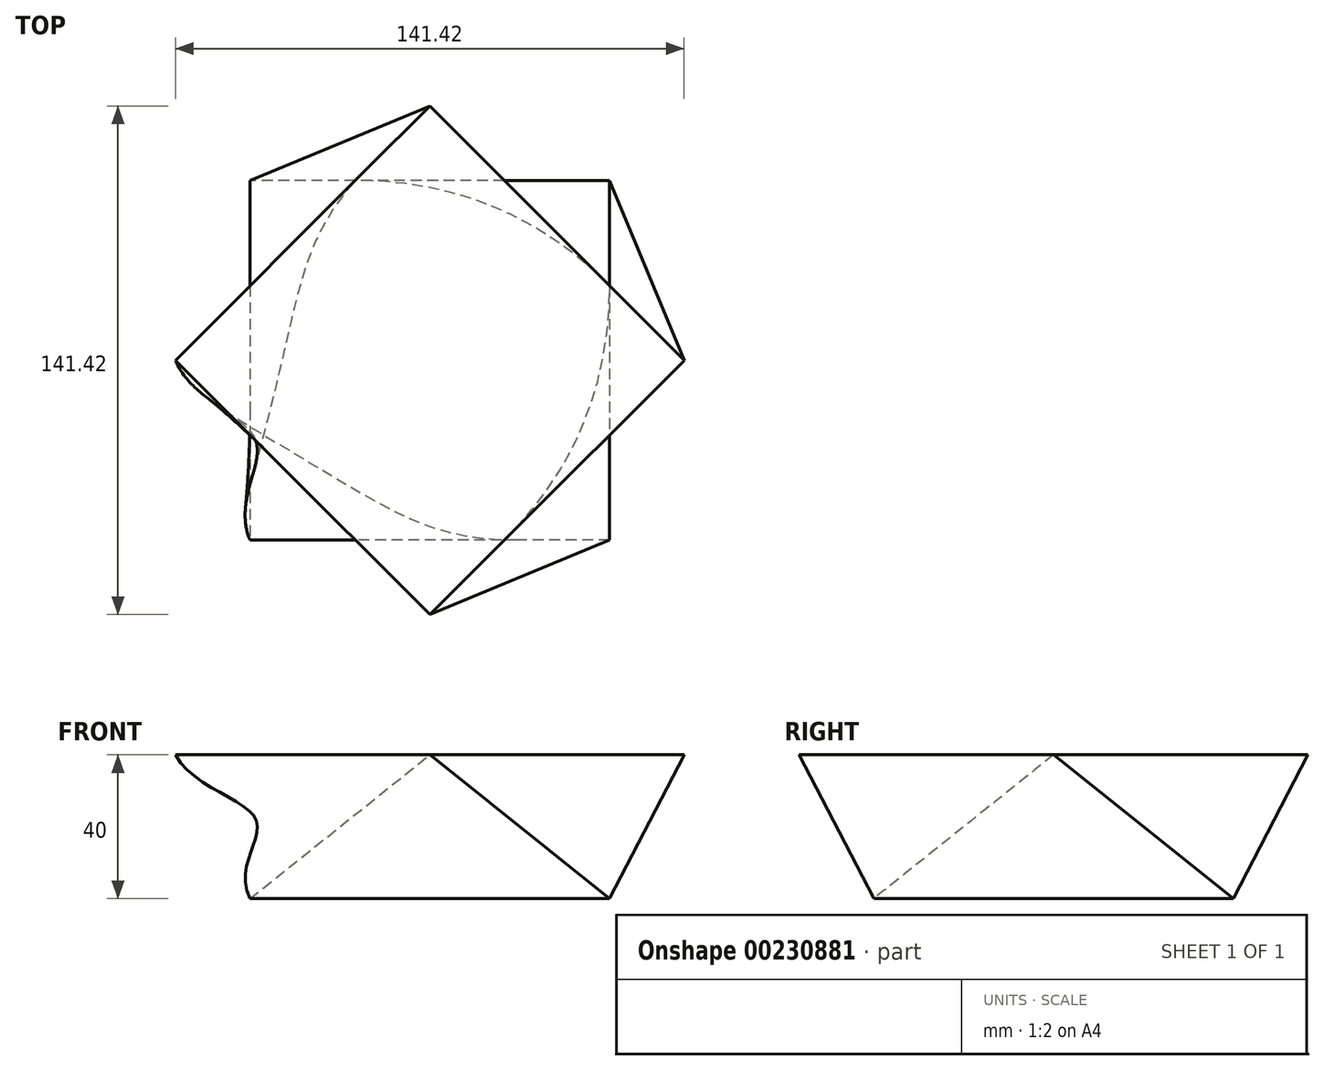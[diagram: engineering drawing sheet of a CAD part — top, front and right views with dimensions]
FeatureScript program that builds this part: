
annotation { "Feature Type Name" : "Feature", "Feature Type Description" : "" }
export const myFeature = defineFeature(function(context is Context, id is Id, definition is map)
    precondition{}
    {
        {
            var Q0;
            Q0=qCreatedBy(makeId("Top.planeOp"),FACE);
            var sketch = newSketch(context, id + "F0", { "sketchPlane" : qUnion([Q0])});
            skLineSegment(sketch, "E0.bottom", {"start": v(50, 50) * mm, "end": v(-50, 50) * mm});
            skLineSegment(sketch, "E0.top", {"start": v(50, -50) * mm, "end": v(-50, -50) * mm});
            skLineSegment(sketch, "E0.left", {"start": v(50, 50) * mm, "end": v(50, -50) * mm});
            skLineSegment(sketch, "E0.right", {"start": v(-50, 50) * mm, "end": v(-50, -50) * mm});
            skPoint(sketch, "E0.middle", {"position": v(0, 0) * mm});
            skSolve(sketch);
        }
        {
            var Q0;
            Q0=qCreatedBy(makeId("Top.planeOp"),FACE);
            cPlane(context, id + "F1", {"entities" : qUnion([Q0]), "cplaneType" : CPlaneType.OFFSET, "offset" : 40 * mm, "width" : 150 * mm, "height" : 150 * mm});
        }
        {
            var Q0;
            Q0=qCreatedBy(id+"F1.planeOp",FACE);
            var sketch = newSketch(context, id + "F2", { "sketchPlane" : qUnion([Q0])});
            skLineSegment(sketch, "E1.bottom", {"start": v(0, -70.71) * mm, "end": v(-70.71, 0) * mm});
            skLineSegment(sketch, "E1.top", {"start": v(70.71, 0) * mm, "end": v(0, 70.71) * mm});
            skLineSegment(sketch, "E1.left", {"start": v(0, -70.71) * mm, "end": v(70.71, 0) * mm});
            skLineSegment(sketch, "E1.right", {"start": v(-70.71, 0) * mm, "end": v(0, 70.71) * mm});
            skPoint(sketch, "E1.middle", {"position": v(0, 0) * mm});
            skSolve(sketch);
        }
        {
            var Q0;
            Q0=sQuery(id+"F2.wireOp",VERTEX,"E1.right.start");
            var Q1;
            Q1=sQuery(id+"F0.wireOp",VERTEX,"E0.right.end");
            var Q2;
            Q2=sQuery(id+"F2.wireOp",VERTEX,"E1.left.end");
            cPlane(context, id + "F3", {"entities" : qUnion([Q0, Q1, Q2]), "cplaneType" : CPlaneType.THREE_POINT, "offset" : 25 * mm, "width" : 150 * mm, "height" : 150 * mm});
        }
        {
            var Q0;
            Q0=qCreatedBy(id+"F3.planeOp",FACE);
            var sketch = newSketch(context, id + "F4", { "sketchPlane" : qUnion([Q0])});
            skPoint(sketch, "E2.0", {"position": v(-70.71, -24.99) * mm});
            skPoint(sketch, "E2.1", {"position": v(-50, 39.04) * mm});
            skLineSegment(sketch, "E3", {"start": v(-70.71, -24.99) * mm, "end": v(-50, 39.04) * mm, "construction": true});
            skLineSegment(sketch, "E4", {"start": v(-48.55, 3.2) * mm, "end": v(-60.36, 7.03) * mm, "construction": true});
            skFitSpline(sketch, "E5", {"points": [v(-70.71, -24.99) * mm, v(-48.55, 3.2) * mm, v(-50, 39.04) * mm], "startDerivative": vector(27.82, 86) * mm, "endDerivative": vector(27.82, 86) * mm});
            skLineSegment(sketch, "E6", {"start": v(-54.64, 24.71) * mm, "end": v(-50, 39.04) * mm, "construction": true});
            skLineSegment(sketch, "E7", {"start": v(-66.07, -10.66) * mm, "end": v(-70.71, -24.99) * mm, "construction": true});
            skSolve(sketch);
        }
        {
            var Q0;
            Q0=qCreatedBy(makeId("Front.planeOp"),FACE);
            var sketch = newSketch(context, id + "F5", { "sketchPlane" : qUnion([Q0])});
            skLineSegment(sketch, "E8", {"start": v(0, 0) * mm, "end": v(0, 40) * mm, "construction": true});
            skSolve(sketch);
        }
        {
            var Q0;
            Q0=makeQuery(id+"F0.imprint","IMPRINT",FACE,{"disambiguationData":[TD([[makeQuery(id+"F0.imprint","IMPRINT",EDGE,{"derivedFrom":sQuery(id+"F0.wireOp",EDGE,"E0.bottom")}),1.0]])]});
            var Q1;
            Q1=makeQuery(id+"F2.imprint","IMPRINT",FACE,{"disambiguationData":[TD([[makeQuery(id+"F2.imprint","IMPRINT",EDGE,{"derivedFrom":sQuery(id+"F2.wireOp",EDGE,"E1.bottom")}),-1.0]])]});
            var Q2;
            Q2=sQuery(id+"F4.wireOp",EDGE,"E5");
            var Q3;
            Q3=sQuery(id+"FdoadWjmi9WGTKn_0.3.F4.wireOp",EDGE,"E5");
            var Q4;
            Q4=sQuery(id+"FdoadWjmi9WGTKn_0.2.F4.wireOp",EDGE,"E5");
            var Q5;
            Q5=sQuery(id+"FdoadWjmi9WGTKn_0.1.F4.wireOp",EDGE,"E5");
            var Q6;
            Q6=sQuery(id+"F4.wireOp",VERTEX,"E2.1");
            var Q7;
            Q7=sQuery(id+"F4.wireOp",VERTEX,"E2.0");
            loft(context, id + "F6", {"addGuides" : true, "sheetProfilesArray" : [{ "sheetProfileEntities" : qUnion([Q0]) }, { "sheetProfileEntities" : qUnion([Q1]) }], "guidesArray" : [{ "guideEntities" : qUnion([Q2]), "guideDerivativeType" : LoftGuideDerivativeType.DEFAULT, "guideDerivativeMagnitude" : 1 }, { "guideEntities" : qUnion([Q3]), "guideDerivativeType" : LoftGuideDerivativeType.DEFAULT, "guideDerivativeMagnitude" : 1 }, { "guideEntities" : qUnion([Q4]), "guideDerivativeType" : LoftGuideDerivativeType.DEFAULT, "guideDerivativeMagnitude" : 1 }, { "guideEntities" : qUnion([Q5]), "guideDerivativeType" : LoftGuideDerivativeType.DEFAULT, "guideDerivativeMagnitude" : 1 }], "matchConnections" : true, "connections" : [{ "connectionEntities" : qUnion([Q6, Q7]), "connectionEdgeQueries" : qUnion([]), "connectionEdgeParameters" : [] }]});
        }
    });
